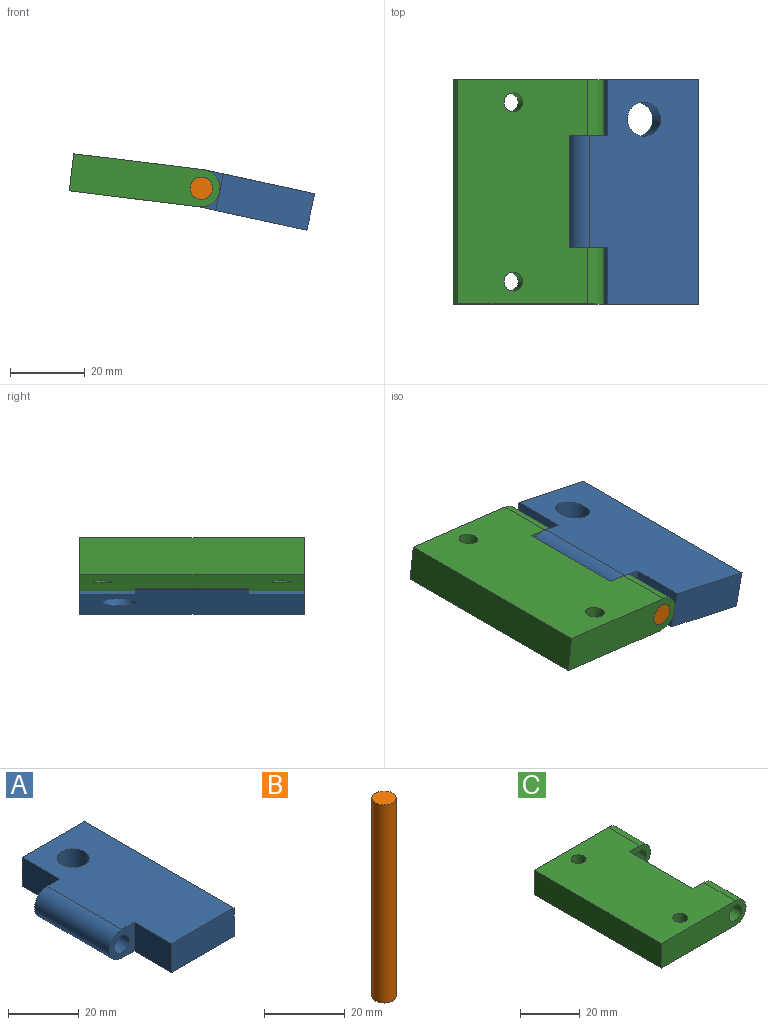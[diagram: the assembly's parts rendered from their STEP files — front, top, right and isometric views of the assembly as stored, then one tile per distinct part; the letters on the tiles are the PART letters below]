
ASSEMBLY  parts=3 mates=2
PART A: 12 faces, bbox 35x60x10 mm
  f0: plane 15x10mm, normal (-1,0,0), area 150mm2, adj f3,f6,f7,f9
  f1: plane 25x10mm, normal (0,-1,0), area 250mm2, adj f2,f5,f6,f7
  f2: plane 60x10mm, normal (1,0,0), area 600mm2, adj f1,f3,f6,f7
  f3: plane 25x10mm, normal (0,1,0), area 250mm2, adj f0,f2,f6,f7
  f4: cylinder r=4.54mm len=10mm, axis (0,0,-1), area 285.5mm2, adj f6,f7
  f5: plane 15x10mm, normal (-1,0,0), area 150mm2, adj f1,f6,f7,f8
  f6: plane 60x30mm, normal (0,0,1), area 1585.1mm2, adj f0,f1,f2,f3,f4,f5,f8,f9
  f7: plane 60x30mm, normal (0,0,-1), area 1585.1mm2, adj f0,f1,f2,f3,f4,f5,f8,f9
  f8: plane 10x10mm, normal (0,-1,0), area 61mm2, adj f5,f6,f7,f10,f11
  f9: plane 10x10mm, normal (0,1,0), area 61mm2, adj f0,f6,f7,f10,f11
  f10: cylinder r=5mm len=30mm, axis (0,-1,0), area 471.2mm2, adj f6,f7,f8,f9
  f11: cylinder r=3mm len=30mm, axis (0,1,0), area 565.5mm2, adj f8,f9
PART B: 3 faces, bbox 6x6x60 mm
  f0: cylinder r=3mm len=60mm, axis (0,0,-1), area 1131mm2, adj f1,f2
  f1: plane 6x6mm, normal (0,0,1), area 28.3mm2, adj f0
  f2: plane 6x6mm, normal (0,0,-1), area 28.3mm2, adj f0
PART C: 14 faces, bbox 40x60x10 mm
  f0: plane 30x10mm, normal (1,0,0), area 300mm2, adj f4,f5,f6,f7
  f1: plane 40x10mm, normal (0,-1,0), area 361mm2, adj f3,f4,f5,f9,f11
  f2: plane 40x10mm, normal (0,1,0), area 361mm2, adj f3,f4,f5,f8,f10
  f3: plane 60x10mm, normal (-1,0,0), area 600mm2, adj f1,f2,f4,f5
  f4: plane 60x35mm, normal (0,0,1), area 1910.7mm2, adj f0,f1,f2,f3,f6,f7,f10,f11
  f5: plane 60x35mm, normal (0,0,-1), area 1910.7mm2, adj f0,f1,f2,f3,f6,f7,f10,f11
  f6: plane 10x10mm, normal (0,1,0), area 61mm2, adj f0,f4,f5,f9,f11
  f7: plane 10x10mm, normal (0,-1,0), area 61mm2, adj f0,f4,f5,f8,f10
  f8: cylinder r=3mm len=15mm, axis (0,-1,0), area 282.7mm2, adj f2,f7
  f9: cylinder r=3mm len=15mm, axis (0,-1,0), area 282.7mm2, adj f1,f6
  f10: cylinder r=5mm len=15mm, axis (0,1,0), area 235.6mm2, adj f2,f4,f5,f7
  f11: cylinder r=5mm len=15mm, axis (0,-1,0), area 235.6mm2, adj f1,f4,f5,f6
  f12: cylinder r=2.5mm len=10mm, axis (0,0,1), area 157.1mm2, adj f4,f5
  f13: cylinder r=2.5mm len=10mm, axis (0,0,1), area 157.1mm2, adj f4,f5
PLACE A rot(axis=(0,1,0),12.2deg) t=(16.04,30,-8.6)mm
PLACE B rot(axis=(1,0,0),90deg) t=(0,60,0)mm
PLACE C rot(axis=(0,1,0),7deg) t=(-20.46,30,-2.54)mm
MATE revolute C.f10 <-> B.f0  axis (0,1,0) through (0,60,0)mm
MATE revolute A.f11 <-> B.f0  axis (0,1,0) through (0,30,0)mm
